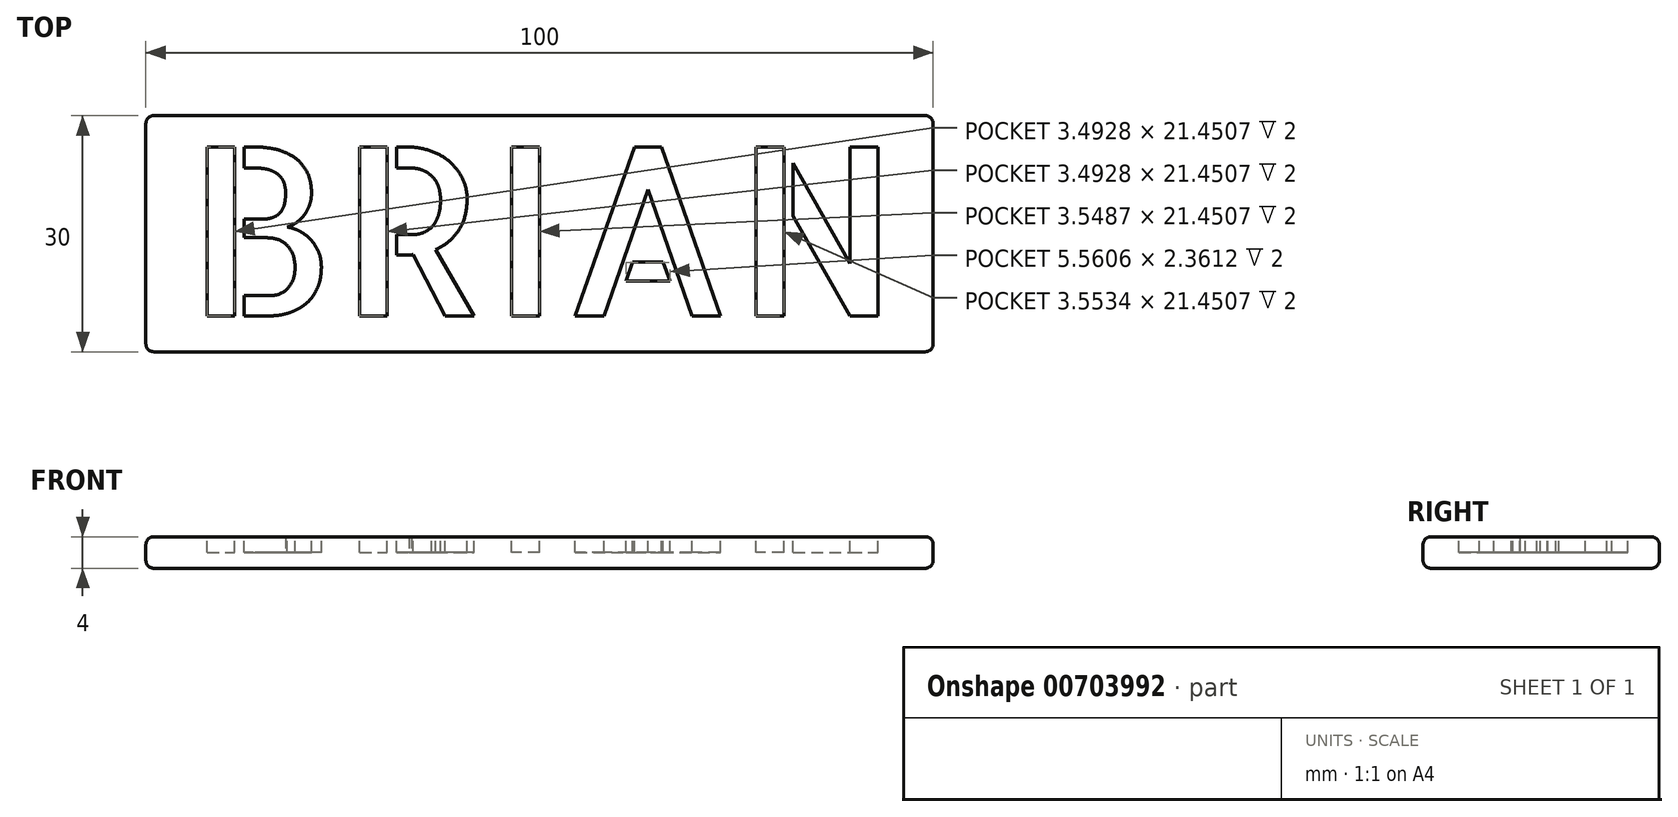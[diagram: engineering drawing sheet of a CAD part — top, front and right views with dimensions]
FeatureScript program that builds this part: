
annotation { "Feature Type Name" : "Feature", "Feature Type Description" : "" }
export const myFeature = defineFeature(function(context is Context, id is Id, definition is map)
    precondition{}
    {
        {
            var Q0;
            Q0=qCreatedBy(makeId("Top.planeOp"),FACE);
            var sketch = newSketch(context, id + "F0", { "sketchPlane" : qUnion([Q0])});
            skLineSegment(sketch, "E0.bottom", {"start": v(50, 15) * mm, "end": v(-50, 15) * mm});
            skLineSegment(sketch, "E0.top", {"start": v(50, -15) * mm, "end": v(-50, -15) * mm});
            skLineSegment(sketch, "E0.left", {"start": v(50, 15) * mm, "end": v(50, -15) * mm});
            skLineSegment(sketch, "E0.right", {"start": v(-50, 15) * mm, "end": v(-50, -15) * mm});
            skPoint(sketch, "E0.middle", {"position": v(0, 0) * mm});
            skSolve(sketch);
        }
        {
            var Q0;
            Q0=makeQuery(id+"F0.imprint","IMPRINT",FACE,{"disambiguationData":[TD([[makeQuery(id+"F0.imprint","IMPRINT",EDGE,{"derivedFrom":sQuery(id+"F0.wireOp",EDGE,"E0.bottom")}),1.0]])]});
            extrude(context, id + "F1", {"entities" : qUnion([Q0]), "oppositeDirection" : true, "depth" : 4 * mm, "offsetDistance" : 25 * mm});
        }
        {
            var Q0;
            Q0=makeQuery(id+"F1.opExtrude","CAP_EDGE",EDGE,{"disambiguationData":[OSD([sQuery(id+"F0.wireOp",EDGE,"E0.bottom")])],"isStart":true});
            var Q1;
            Q1=makeQuery(id+"F1.opExtrude","CAP_EDGE",EDGE,{"disambiguationData":[OSD([sQuery(id+"F0.wireOp",EDGE,"E0.bottom")])],"isStart":false});
            var Q2;
            Q2=makeQuery(id+"F1.opExtrude","CAP_EDGE",EDGE,{"disambiguationData":[OSD([sQuery(id+"F0.wireOp",EDGE,"E0.right")])],"isStart":true});
            var Q3;
            Q3=makeQuery(id+"F1.opExtrude","CAP_EDGE",EDGE,{"disambiguationData":[OSD([sQuery(id+"F0.wireOp",EDGE,"E0.right")])],"isStart":false});
            var Q4;
            Q4=makeQuery(id+"F1.opExtrude","SWEPT_EDGE",EDGE,{"disambiguationData":[OSD([sQuery(id+"F0.wireOp",EDGE,"E0.bottom"),sQuery(id+"F0.wireOp",EDGE,"E0.right")])]});
            var Q5;
            Q5=makeQuery(id+"F1.opExtrude","SWEPT_EDGE",EDGE,{"disambiguationData":[OSD([sQuery(id+"F0.wireOp",EDGE,"E0.bottom"),sQuery(id+"F0.wireOp",EDGE,"E0.left")])]});
            var Q6;
            Q6=makeQuery(id+"F1.opExtrude","CAP_EDGE",EDGE,{"disambiguationData":[OSD([sQuery(id+"F0.wireOp",EDGE,"E0.left")])],"isStart":false});
            var Q7;
            Q7=makeQuery(id+"F1.opExtrude","CAP_EDGE",EDGE,{"disambiguationData":[OSD([sQuery(id+"F0.wireOp",EDGE,"E0.left")])],"isStart":true});
            var Q8;
            Q8=makeQuery(id+"F1.opExtrude","SWEPT_EDGE",EDGE,{"disambiguationData":[OSD([sQuery(id+"F0.wireOp",EDGE,"E0.top"),sQuery(id+"F0.wireOp",EDGE,"E0.left")])]});
            var Q9;
            Q9=makeQuery(id+"F1.opExtrude","CAP_EDGE",EDGE,{"disambiguationData":[OSD([sQuery(id+"F0.wireOp",EDGE,"E0.top")])],"isStart":false});
            var Q10;
            Q10=makeQuery(id+"F1.opExtrude","CAP_EDGE",EDGE,{"disambiguationData":[OSD([sQuery(id+"F0.wireOp",EDGE,"E0.top")])],"isStart":true});
            var Q11;
            Q11=makeQuery(id+"F1.opExtrude","SWEPT_EDGE",EDGE,{"disambiguationData":[OSD([sQuery(id+"F0.wireOp",EDGE,"E0.top"),sQuery(id+"F0.wireOp",EDGE,"E0.right")])]});
            fillet(context, id + "F2", {"entities" : qUnion([Q0, Q1, Q2, Q3, Q4, Q5, Q6, Q7, Q8, Q9, Q10, Q11]), "radius" : 1 * mm, "tangentPropagation" : true, "allowEdgeOverflow" : false});
        }
        {
            var Q0;
            Q0=qCreatedBy(makeId("Top.planeOp"),FACE);
            var sketch = newSketch(context, id + "F3", { "sketchPlane" : qUnion([Q0])});
            skText(sketch, "E1", { "text": "BRIAN", "fontName": "AllertaStencil-Regular.ttf"});
            const initialGuessF3  = {"E1": [-0.045, -0.01044, 1, 0, 0.02146]};
            skSetInitialGuess(sketch, initialGuessF3);
            skSolve(sketch);
        }
        {
            var Q0;
            Q0 = qSketchRegion(id + "F3", true);
            extrude(context, id + "F4", {"entities" : qUnion([Q0]), "operationType" : NewBodyOperationType.REMOVE, "oppositeDirection" : true, "depth" : 2 * mm, "offsetDistance" : 25 * mm});
        }
    });
